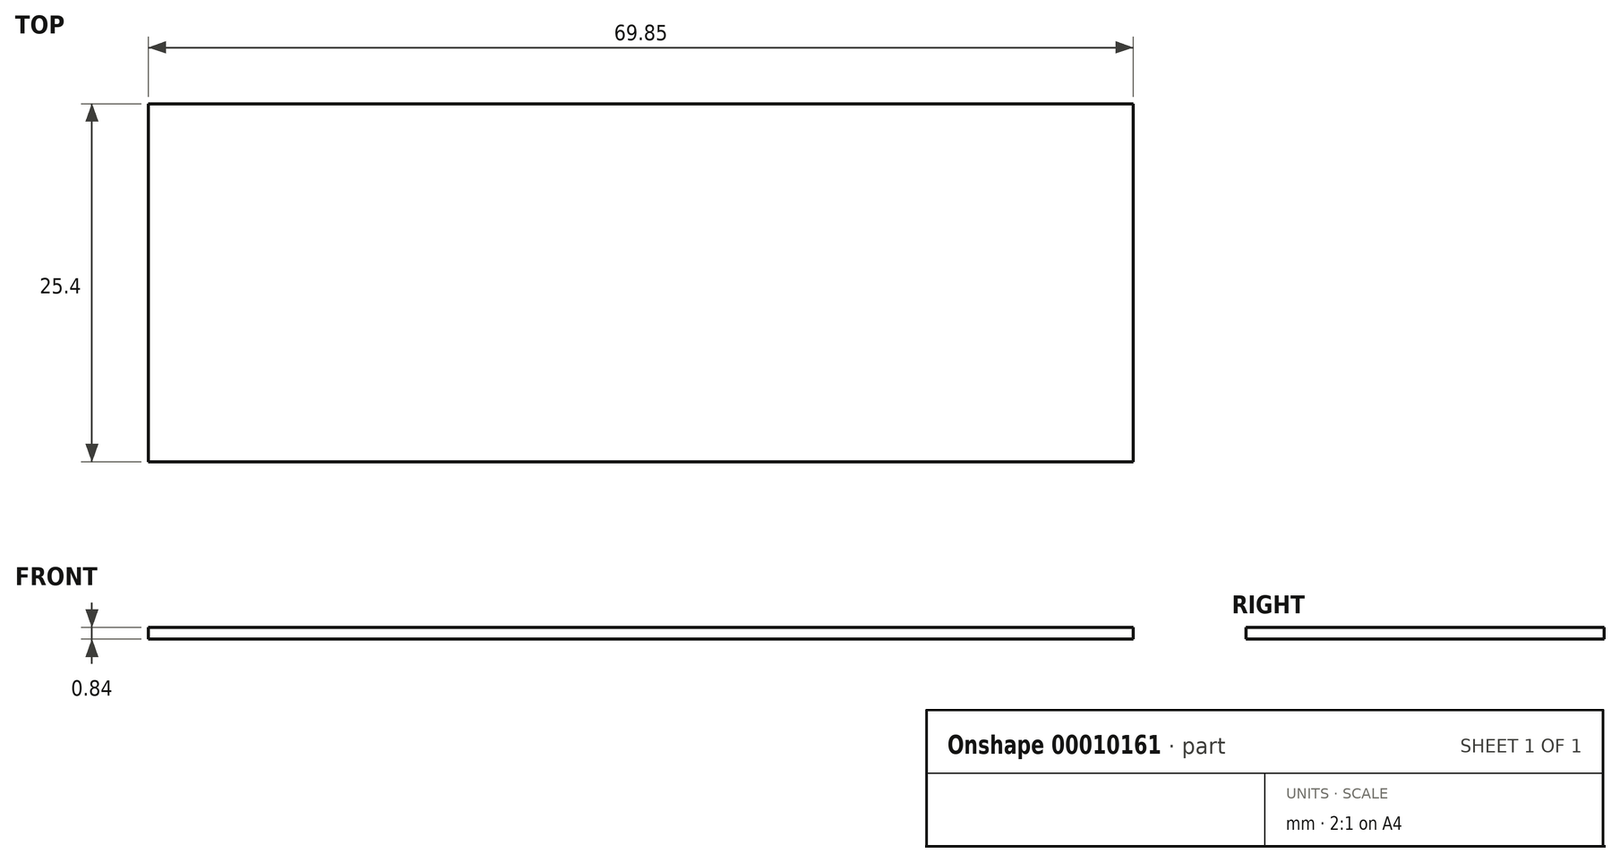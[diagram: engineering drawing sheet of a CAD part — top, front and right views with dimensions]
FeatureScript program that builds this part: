
annotation { "Feature Type Name" : "Feature", "Feature Type Description" : "" }
export const myFeature = defineFeature(function(context is Context, id is Id, definition is map)
    precondition{}
    {
        {
            var Q0;
            Q0=qCreatedBy(makeId("Right.planeOp"),FACE);
            var sketch = newSketch(context, id + "F0", { "sketchPlane" : qUnion([Q0])});
            skLineSegment(sketch, "E0.rect.bottom", {"start": v(12.7, 0.42) * mm, "end": v(-12.7, 0.42) * mm});
            skLineSegment(sketch, "E0.rect.top", {"start": v(12.7, -0.42) * mm, "end": v(-12.7, -0.42) * mm});
            skLineSegment(sketch, "E0.rect.left", {"start": v(12.7, 0.42) * mm, "end": v(12.7, -0.42) * mm});
            skLineSegment(sketch, "E0.rect.right", {"start": v(-12.7, 0.42) * mm, "end": v(-12.7, -0.42) * mm});
            skPoint(sketch, "E0.rect.middle", {"position": v(0, 0) * mm});
            skSolve(sketch);
        }
        {
            var Q0;
            Q0 = qSketchRegion(id + "F0", true);
            extrude(context, id + "F1", {"entities" : qUnion([Q0]), "depth" : 69.85 * mm});
        }
    });
